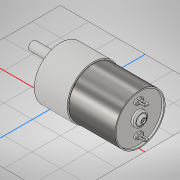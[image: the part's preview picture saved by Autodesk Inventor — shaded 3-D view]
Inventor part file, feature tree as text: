
AUTODESK INVENTOR PART (.ipt)
format: ipt  version: 2022 (Build 260153000, 153)  size: 283,136 bytes
history: native  units: mm
features: sketch x2, projected_geometry x2, extrude x1, other x1
ambient origin geometry x8: Origin, YZ Plane, XZ Plane, XY Plane, X Axis, Y Axis, Z Axis, Center Point
bodies: Solid1 (feature_tree)
feature tree (6):
  sketch  "Sketch1"  dims[d0=8.0mm d1=45.75mm d2=0.0mm]
  extrude  "Extrusion1"  Depth=45.75mm TaperAngle=0.0deg
  projected_geometry  "Projected Loop1"
  projected_geometry  "Projected Loop2"
  sketch  "Sketch2"
  other  "Aynalama2"
